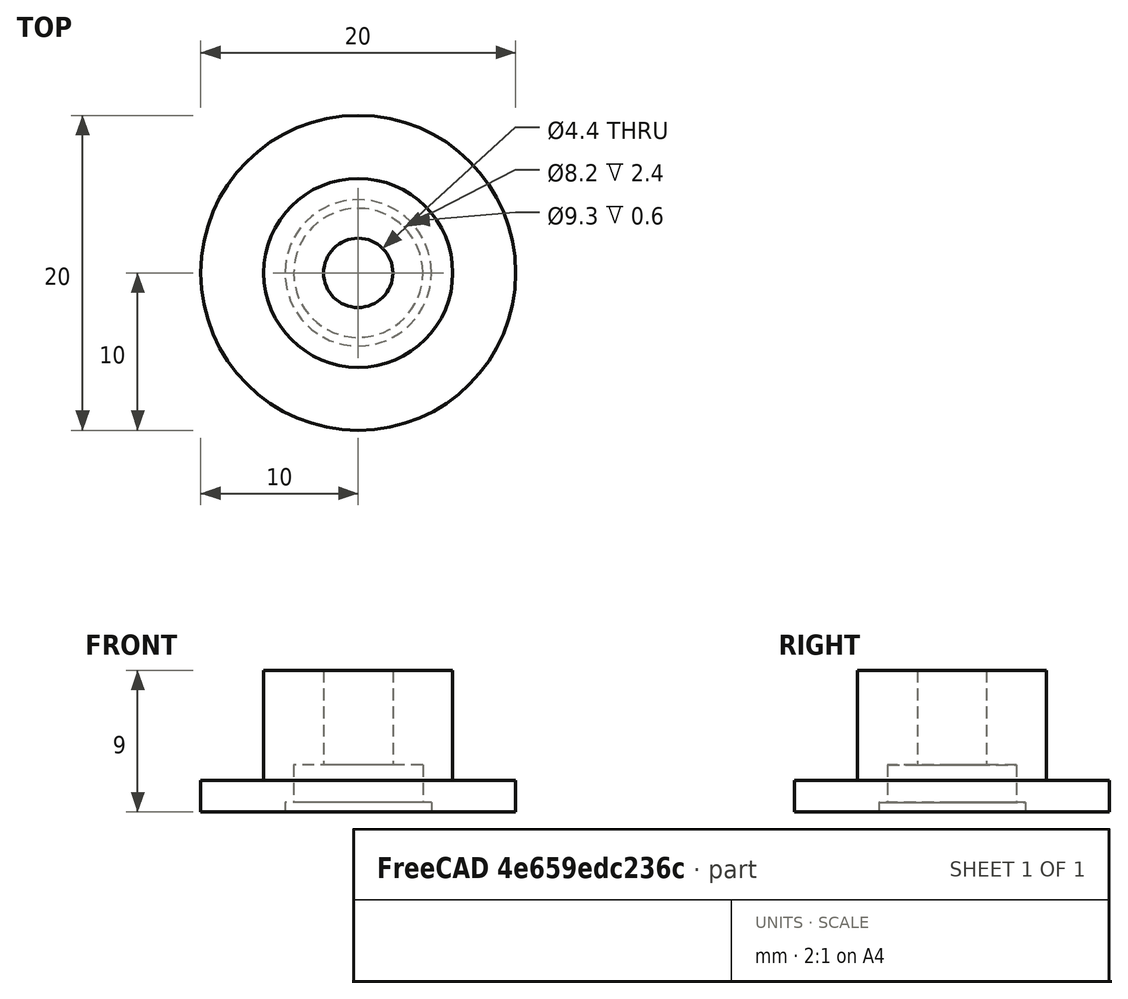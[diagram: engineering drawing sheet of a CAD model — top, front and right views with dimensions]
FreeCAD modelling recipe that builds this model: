
FCSTD DOCUMENT  (FreeCAD 0.16R6458 (Git))
Label: Art3TensionerPulley
License: CreativeCommons Attribution-ShareAlike
LicenseURL: http://creativecommons.org/licenses/by-sa/4.0/
objects: Sketcher::SketchObject×1, PartDesign::Revolution×1
note: 3 computed .brp shape members not serialized (recipe doc carries the construction recipe); baked Part::Feature solids carry a one-line shape summary decoded from their .brp

FEATURE [Sketcher::SketchObject] Sketch
  Placement = pos=(0,0,0) rot=(1,0,0;1.5708rad)
  sketch-geometry (10):
    g0: LineSegment StartX=4.65 StartY=0 StartZ=0 EndX=10 EndY=0 EndZ=0
    g1: LineSegment StartX=10 StartY=0 StartZ=0 EndX=10 EndY=2 EndZ=0
    g2: LineSegment StartX=10 StartY=2 StartZ=0 EndX=6 EndY=2 EndZ=0
    g3: LineSegment StartX=6 StartY=2 StartZ=0 EndX=6 EndY=9 EndZ=0
    g4: LineSegment StartX=6 StartY=9 StartZ=0 EndX=2.2 EndY=9 EndZ=0
    g5: LineSegment StartX=2.2 StartY=9 StartZ=0 EndX=2.2 EndY=3 EndZ=0
    g6: LineSegment StartX=2.2 StartY=3 StartZ=0 EndX=4.1 EndY=3 EndZ=0
    g7: LineSegment StartX=4.1 StartY=3 StartZ=0 EndX=4.1 EndY=0.6 EndZ=0
    g8: LineSegment StartX=4.1 StartY=0.6 StartZ=0 EndX=4.65 EndY=0.6 EndZ=0
    g9: LineSegment StartX=4.65 StartY=0.6 StartZ=0 EndX=4.65 EndY=0 EndZ=0
  constraints (30):
    c: PointOnObject(g0,g-1)
    c: Horizontal(g0)
    c: Coincident(g0,g1)
    c: Vertical(g1)
    c: Coincident(g1,g2)
    c: Horizontal(g2)
    c: Coincident(g2,g3)
    c: Vertical(g3)
    c: Coincident(g3,g4)
    c: Horizontal(g4)
    c: Coincident(g4,g5)
    c: Vertical(g5)
    c: Coincident(g5,g6)
    c: Horizontal(g6)
    c: Coincident(g6,g7)
    c: Vertical(g7)
    c: Coincident(g7,g8)
    c: Horizontal(g8)
    c: Coincident(g8,g9)
    c: Coincident(g9,g0)
    c: Vertical(g9)
    c: DistanceX(g-1,g0) = 10
    c: DistanceX(g-1,g4) = 2.2
    c: DistanceX(g-1,g3) = 6
    c: DistanceY(g1) = 2
    c: DistanceY(g-1,g6) = 3
    c: DistanceY(g9) = -0.6
    c: DistanceX(g-1,g0) = 4.65
    c: DistanceX(g-1,g7) = 4.1
    c: DistanceY(g-1,g3) = 9
FEATURE [PartDesign::Revolution] Revolution  label="Art3TensionerPulley"
  Angle = 360
  Axis = (0,0,1)
  Base = (0,0,0)
  Placement = pos=(0,0,0) rot=(1,0,0;1.5708rad)
  ReferenceAxis = -> Sketch [V_Axis]
  Reversed = true
  Sketch = -> Sketch
